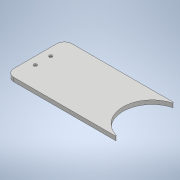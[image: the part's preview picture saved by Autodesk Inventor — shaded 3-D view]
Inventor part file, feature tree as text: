
AUTODESK INVENTOR PART (.ipt)
format: ipt  version: 2020 (Build 240168000, 168)  size: 127,488 bytes
history: native  units: mm
features: fillet x2, extrude x1, hole x1, sketch x1
ambient origin geometry x8: Origin, YZ Plane, XZ Plane, XY Plane, X Axis, Y Axis, Z Axis, Center Point
bodies: Body1 (feature_tree)
feature tree (5):
  extrude  "Выдавливание3"  Depth=13.25mm
  fillet  "Сопряжение3"  Radius=1.8mm
  fillet  "Сопряжение4"  Radius=40.0mm
  hole  "Отверстие1"  [1 undecoded]
  sketch  "Эскиз6"
note: 1 required parameter value undecoded (feature->parameter linkage not recoverable at this tier; creation-order binding heuristic only, values carry confidence <= 0.55)
